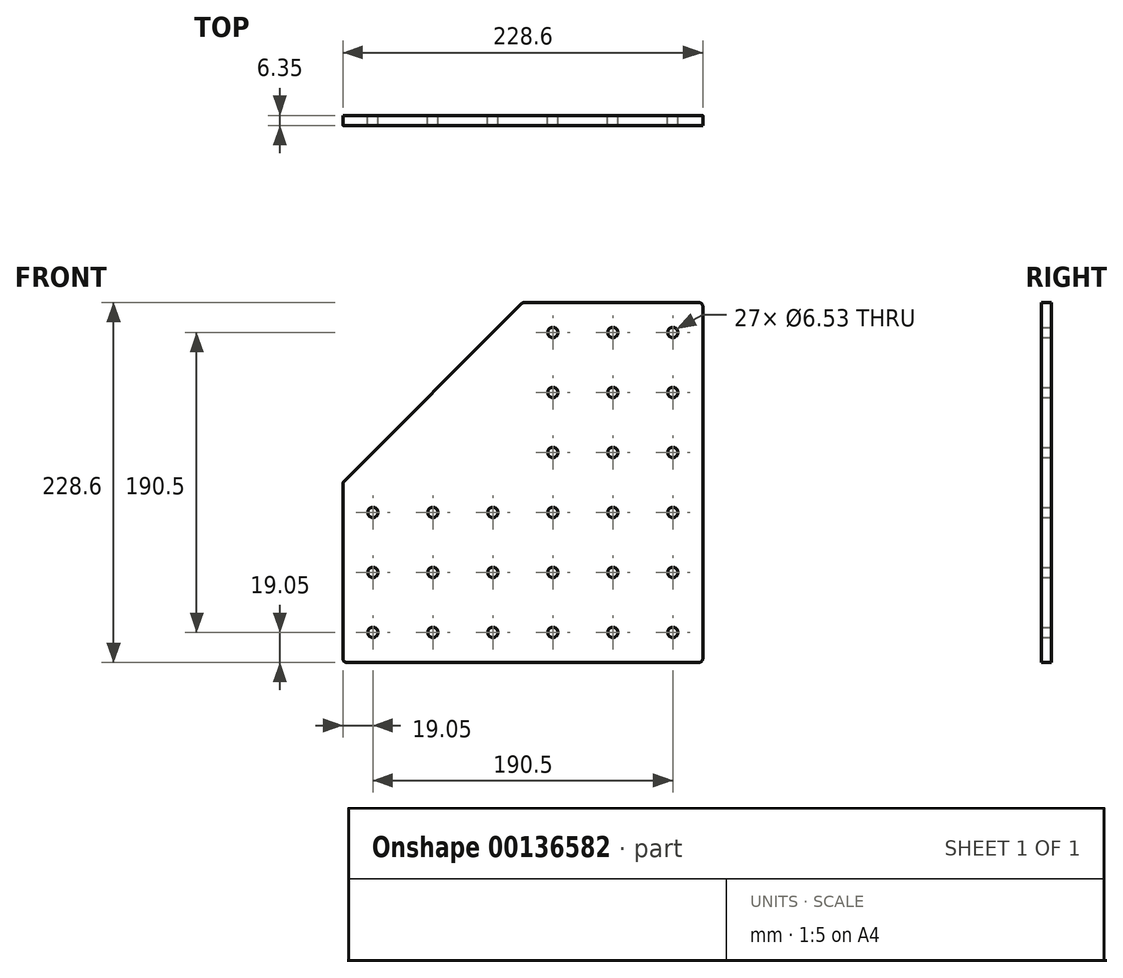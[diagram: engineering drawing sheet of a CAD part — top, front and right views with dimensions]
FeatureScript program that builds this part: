
annotation { "Feature Type Name" : "Feature", "Feature Type Description" : "" }
export const myFeature = defineFeature(function(context is Context, id is Id, definition is map)
    precondition{}
    {
        {
            var Q0;
            Q0=qCreatedBy(makeId("Front.planeOp"),FACE);
            var sketch = newSketch(context, id + "F0", { "sketchPlane" : qUnion([Q0])});
            skLineSegment(sketch, "E0.bottom", {"start": v(2.54, 0) * mm, "end": v(226.06, 0) * mm});
            skLineSegment(sketch, "E0.top", {"start": v(0, 114.3) * mm, "end": v(228.6, 114.3) * mm, "construction": true});
            skLineSegment(sketch, "E0.left", {"start": v(0, 2.54) * mm, "end": v(0, 113.25) * mm});
            skLineSegment(sketch, "E0.right", {"start": v(228.6, 2.54) * mm, "end": v(228.6, 114.3) * mm});
            skLineSegment(sketch, "E1.bottom", {"start": v(228.6, 114.3) * mm, "end": v(114.3, 114.3) * mm, "construction": true});
            skLineSegment(sketch, "E1.top", {"start": v(226.06, 228.6) * mm, "end": v(115.35, 228.6) * mm});
            skLineSegment(sketch, "E1.left", {"start": v(228.6, 114.3) * mm, "end": v(228.6, 226.06) * mm});
            skLineSegment(sketch, "E1.right", {"start": v(114.3, 114.3) * mm, "end": v(114.3, 228.6) * mm, "construction": true});
            skLineSegment(sketch, "E2", {"start": v(0.74, 115.04) * mm, "end": v(113.56, 227.86) * mm});
            skCircle(sketch, "E3", {"center": v(209.55, 209.55) * mm, "radius": 3.26 * mm});
            skCircle(sketch, "E4.0.1.0", {"center": v(209.55, 171.45) * mm, "radius": 3.26 * mm});
            skCircle(sketch, "E4.0.2.0", {"center": v(209.55, 133.35) * mm, "radius": 3.26 * mm});
            skCircle(sketch, "E4.0.3.0", {"center": v(209.55, 95.25) * mm, "radius": 3.26 * mm});
            skCircle(sketch, "E4.0.4.0", {"center": v(209.55, 57.15) * mm, "radius": 3.26 * mm});
            skCircle(sketch, "E4.0.5.0", {"center": v(209.55, 19.05) * mm, "radius": 3.26 * mm});
            skCircle(sketch, "E4.1.0.0", {"center": v(171.45, 209.55) * mm, "radius": 3.26 * mm});
            skCircle(sketch, "E4.1.1.0", {"center": v(171.45, 171.45) * mm, "radius": 3.26 * mm});
            skCircle(sketch, "E4.1.2.0", {"center": v(171.45, 133.35) * mm, "radius": 3.26 * mm});
            skCircle(sketch, "E4.1.3.0", {"center": v(171.45, 95.25) * mm, "radius": 3.26 * mm});
            skCircle(sketch, "E4.1.4.0", {"center": v(171.45, 57.15) * mm, "radius": 3.26 * mm});
            skCircle(sketch, "E4.1.5.0", {"center": v(171.45, 19.05) * mm, "radius": 3.26 * mm});
            skLineSegment(sketch, "E4.direction1", {"start": v(209.55, 209.55) * mm, "end": v(171.45, 209.55) * mm, "construction": true});
            skLineSegment(sketch, "E4.direction2", {"start": v(209.55, 209.55) * mm, "end": v(209.55, 171.45) * mm, "construction": true});
            skCircle(sketch, "E5", {"center": v(19.05, 95.25) * mm, "radius": 3.26 * mm});
            skCircle(sketch, "E6.0.1.0", {"center": v(19.05, 57.15) * mm, "radius": 3.26 * mm});
            skCircle(sketch, "E6.0.2.0", {"center": v(19.05, 19.05) * mm, "radius": 3.26 * mm});
            skCircle(sketch, "E6.1.0.0", {"center": v(57.15, 95.25) * mm, "radius": 3.26 * mm});
            skCircle(sketch, "E6.1.1.0", {"center": v(57.15, 57.15) * mm, "radius": 3.26 * mm});
            skCircle(sketch, "E6.1.2.0", {"center": v(57.15, 19.05) * mm, "radius": 3.26 * mm});
            skCircle(sketch, "E6.2.0.0", {"center": v(95.25, 95.25) * mm, "radius": 3.26 * mm});
            skCircle(sketch, "E6.2.1.0", {"center": v(95.25, 57.15) * mm, "radius": 3.26 * mm});
            skCircle(sketch, "E6.2.2.0", {"center": v(95.25, 19.05) * mm, "radius": 3.26 * mm});
            skCircle(sketch, "E6.3.0.0", {"center": v(133.35, 95.25) * mm, "radius": 3.26 * mm});
            skCircle(sketch, "E6.3.1.0", {"center": v(133.35, 57.15) * mm, "radius": 3.26 * mm});
            skCircle(sketch, "E6.3.2.0", {"center": v(133.35, 19.05) * mm, "radius": 3.26 * mm});
            skLineSegment(sketch, "E6.direction1", {"start": v(19.05, 95.25) * mm, "end": v(57.15, 95.25) * mm, "construction": true});
            skLineSegment(sketch, "E6.direction2", {"start": v(19.05, 95.25) * mm, "end": v(19.05, 57.15) * mm, "construction": true});
            skPoint(sketch, "E7.visualSharp", {"position": v(0, 114.3) * mm});
            skArc(sketch, "E7.filletArc", {"start": v(0.74, 115.04) * mm, "mid": v(0.2, 114.22) * mm, "end": v(0, 113.25) * mm});
            skPoint(sketch, "E8.visualSharp", {"position": v(114.3, 228.6) * mm});
            skArc(sketch, "E8.filletArc", {"start": v(115.35, 228.6) * mm, "mid": v(114.38, 228.4) * mm, "end": v(113.56, 227.86) * mm});
            skPoint(sketch, "E9.visualSharp", {"position": v(228.6, 228.6) * mm});
            skArc(sketch, "E9.filletArc", {"start": v(228.6, 226.06) * mm, "mid": v(227.86, 227.86) * mm, "end": v(226.06, 228.6) * mm});
            skPoint(sketch, "E10.visualSharp", {"position": v(228.6, 0) * mm});
            skArc(sketch, "E10.filletArc", {"start": v(226.06, 0) * mm, "mid": v(227.86, 0.74) * mm, "end": v(228.6, 2.54) * mm});
            skPoint(sketch, "E11.visualSharp", {"position": v(0, 0) * mm});
            skArc(sketch, "E11.filletArc", {"start": v(0, 2.54) * mm, "mid": v(0.74, 0.74) * mm, "end": v(2.54, 0) * mm});
            skCircle(sketch, "E12.0.2.0", {"center": v(133.35, 209.55) * mm, "radius": 3.26 * mm});
            skCircle(sketch, "E12.0.2.1", {"center": v(133.35, 171.45) * mm, "radius": 3.26 * mm});
            skCircle(sketch, "E12.0.2.2", {"center": v(133.35, 133.35) * mm, "radius": 3.26 * mm});
            skSolve(sketch);
        }
        {
            var Q0;
            Q0=makeQuery(id+"F0.imprint","IMPRINT",FACE,{"disambiguationData":[TD([[makeQuery(id+"F0.imprint","IMPRINT",EDGE,{"derivedFrom":sQuery(id+"F0.wireOp",EDGE,"E0.bottom")}),1.0]])]});
            extrude(context, id + "F1", {"entities" : qUnion([Q0]), "depth" : 6.35 * mm});
        }
    });
